# Revit family: Energy_Recovery-Ventilator-WEHC-ARR6
name_source: partatom
category: Mechanical Equipment
revit_build: Autodesk Revit MEP 2012 (Build: 20110916_2132(x64)
units: mm (PartAtom-declared; Revit-internal decimal feet)

## types (1)
- Energy_Recovery-Ventilator-WEHC-ARR6
    D1 = 32"
    D2 = 12"
    D3 = 13"
    D4 = 27"
    Default Elevation = 0"
    Description = Energy Recovery Ventilator
    Duct Arrangement = 6
    Exhaust Height = 8 1/2"
    Exhaust Location From Bottom = 6 1/2"
    Exhaust Location From End = 4 1/8"
    Exhaust Width = 7 1/8"
    Height of Unit = 32"
    Intake Height = 10"
    Intake Location From Bottom = 6"
    Intake Location From Side = 6 3/4"
    Intake Width = 8"
    Length of Unit = 49"
    Manufacturer = CARNES COMPANY
    Manufacturer Fax = 608-845-6470
    Model = WEHC-ARR6-01
    Return Height = 10"
    Return Location From Bottom = 6"
    Return Location From Side = 7"
    Return Width = 8"
    Size = 1
    Subcategory = Ventilation
    URL = www.carnes.com/
    Unit = Metal - Carnes - Aluminum Frame - Painted White
    Weight = 550
    Width of Unit = 32"

## geometry (parser evidence)
native form markers: Blend x4, Sweep x13
no freeform markers — native parametric forms only
